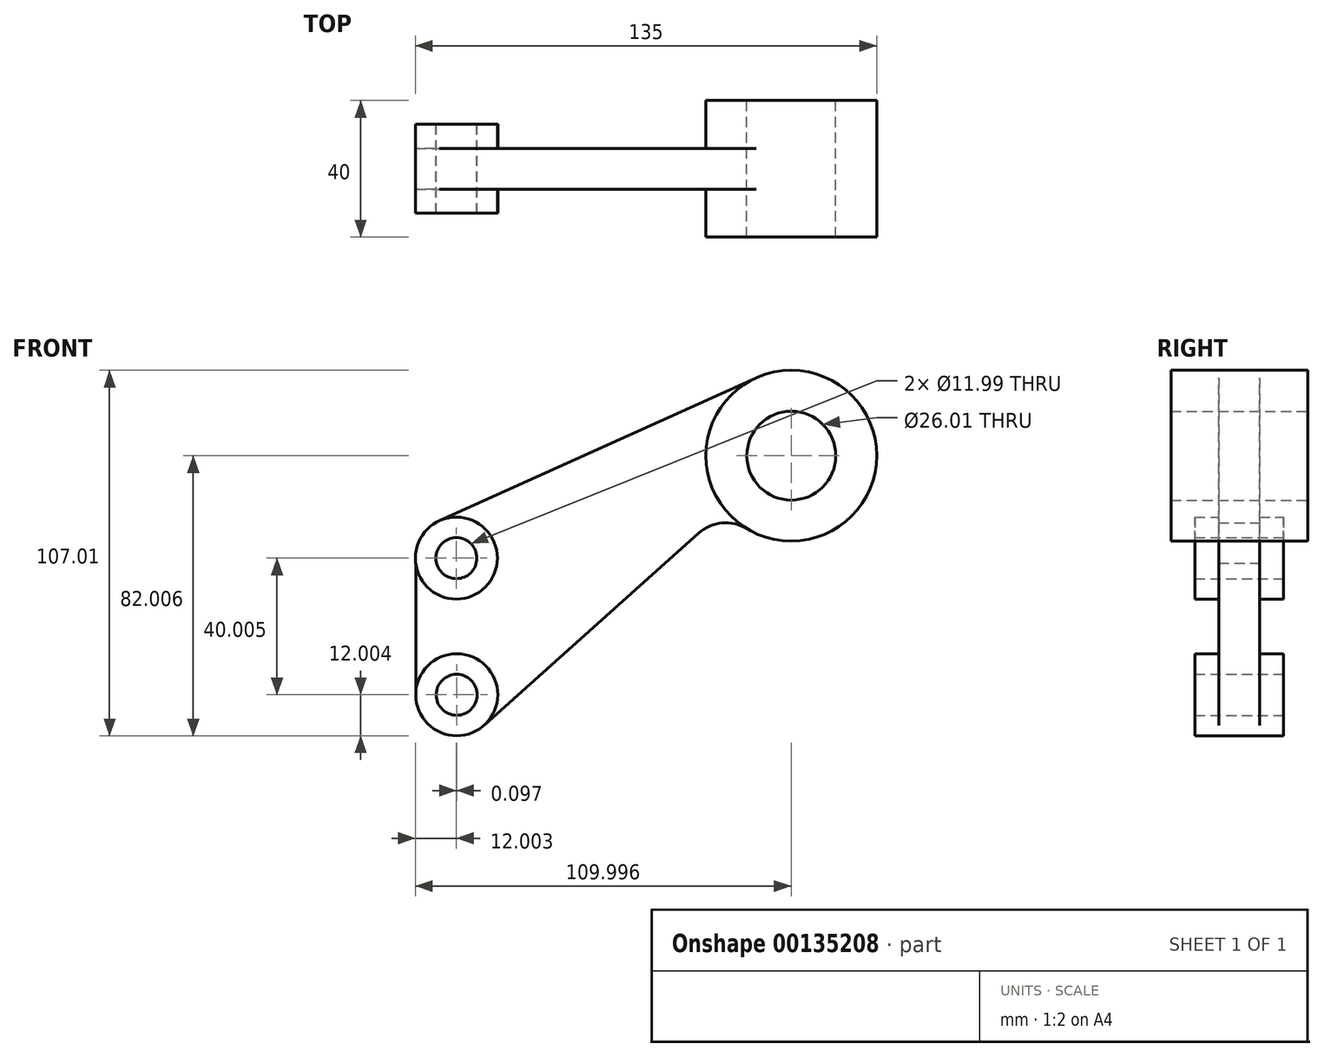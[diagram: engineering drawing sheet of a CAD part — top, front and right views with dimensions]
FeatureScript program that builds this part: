
annotation { "Feature Type Name" : "Feature", "Feature Type Description" : "" }
export const myFeature = defineFeature(function(context is Context, id is Id, definition is map)
    precondition{}
    {
        {
            var Q0;
            Q0=qCreatedBy(makeId("Front.planeOp"),FACE);
            var sketch = newSketch(context, id + "F0", { "sketchPlane" : qUnion([Q0])});
            skCircle(sketch, "E0", {"center": v(-75, 17.6) * mm, "radius": 12 * mm});
            skCircle(sketch, "E1", {"center": v(-74.9, -22.4) * mm, "radius": 12 * mm});
            skCircle(sketch, "E2", {"center": v(23, 47.6) * mm, "radius": 25 * mm});
            skLineSegment(sketch, "E3", {"start": v(-79.94, 28.54) * mm, "end": v(12.7, 70.38) * mm});
            skLineSegment(sketch, "E4", {"start": v(-86.9, 16.08) * mm, "end": v(-86.9, -22.4) * mm});
            skArc(sketch, "E5", {"start": v(10.05, 26.2) * mm, "mid": v(2.72, 27.88) * mm, "end": v(-4.16, 24.88) * mm});
            skLineSegment(sketch, "E6", {"start": v(-66.9, -31.34) * mm, "end": v(-4.16, 24.88) * mm});
            skCircle(sketch, "E7", {"center": v(-75, 17.6) * mm, "radius": 6 * mm});
            skCircle(sketch, "E8", {"center": v(-74.9, -22.4) * mm, "radius": 6 * mm});
            skCircle(sketch, "E9", {"center": v(23, 47.6) * mm, "radius": 13 * mm});
            skSolve(sketch);
        }
        {
            var Q0;
            {var subQ0=sQuery(id+"F0.wireOp",EDGE,"E3");Q0=makeQuery(id+"F0.imprint","IMPRINT",FACE,{"disambiguationData":[TD([[makeQuery(id+"F0.imprint","IMPRINT",EDGE,{"derivedFrom":subQ0}),-1.0]])]});}
            extrude(context, id + "F1", {"entities" : qUnion([Q0]), "endBound" : BoundingType.SYMMETRIC, "depth" : 12 * mm});
        }
        {
            var Q0;
            Q0=makeQuery(id+"F0.imprint","IMPRINT",FACE,{"disambiguationData":[TD([[makeQuery(id+"F0.imprint","IMPRINT",EDGE,{"derivedFrom":sQuery(id+"F0.wireOp",EDGE,"E9")}),-1.0]])]});
            extrude(context, id + "F2", {"entities" : qUnion([Q0]), "operationType" : NewBodyOperationType.ADD, "endBound" : BoundingType.SYMMETRIC, "depth" : 40 * mm});
        }
        {
            var Q0;
            Q0=makeQuery(id+"F0.imprint","IMPRINT",FACE,{"disambiguationData":[TD([[makeQuery(id+"F0.imprint","IMPRINT",EDGE,{"derivedFrom":sQuery(id+"F0.wireOp",EDGE,"E7")}),-1.0]])]});
            var Q1;
            Q1=makeQuery(id+"F0.imprint","IMPRINT",FACE,{"disambiguationData":[TD([[makeQuery(id+"F0.imprint","IMPRINT",EDGE,{"derivedFrom":sQuery(id+"F0.wireOp",EDGE,"E8")}),-1.0]])]});
            extrude(context, id + "F3", {"entities" : qUnion([Q0, Q1]), "operationType" : NewBodyOperationType.ADD, "endBound" : BoundingType.SYMMETRIC, "depth" : 26 * mm});
        }
    });
